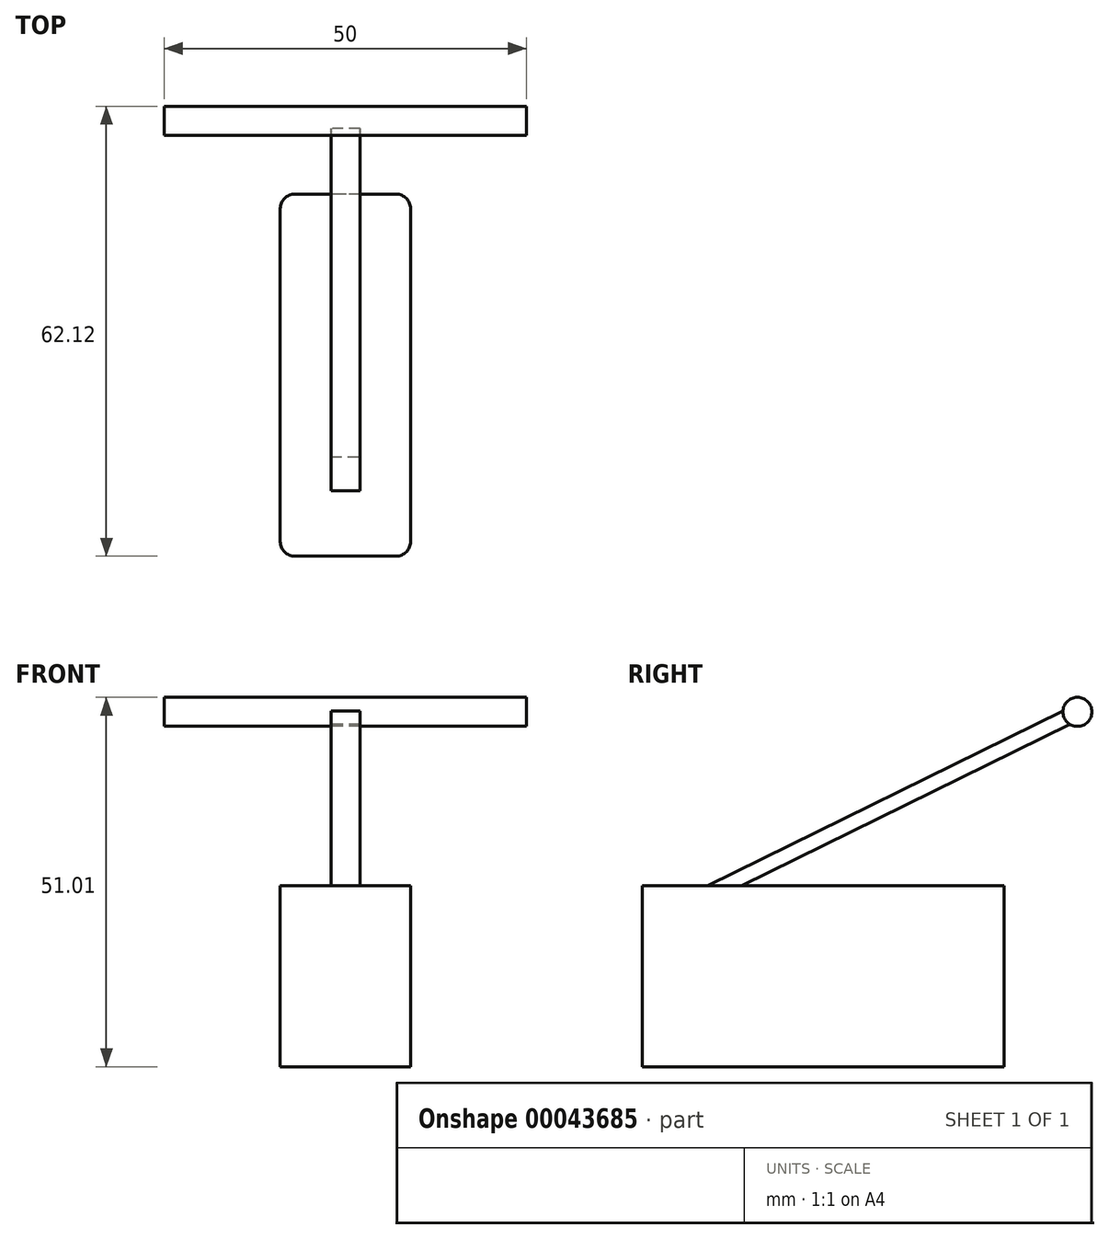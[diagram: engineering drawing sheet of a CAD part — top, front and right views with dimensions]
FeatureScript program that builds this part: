
annotation { "Feature Type Name" : "Feature", "Feature Type Description" : "" }
export const myFeature = defineFeature(function(context is Context, id is Id, definition is map)
    precondition{}
    {
        {
            var Q0;
            Q0=qCreatedBy(makeId("Top.planeOp"),FACE);
            var sketch = newSketch(context, id + "F0", { "sketchPlane" : qUnion([Q0])});
            skLineSegment(sketch, "E0.rect.bottom", {"start": v(7, -25) * mm, "end": v(-7, -25) * mm});
            skLineSegment(sketch, "E0.rect.top", {"start": v(7, 25) * mm, "end": v(-7, 25) * mm});
            skLineSegment(sketch, "E0.rect.left", {"start": v(9, -23) * mm, "end": v(9, 23) * mm});
            skLineSegment(sketch, "E0.rect.right", {"start": v(-9, -23) * mm, "end": v(-9, 23) * mm});
            skPoint(sketch, "E0.rect.middle", {"position": v(0, 0) * mm});
            skPoint(sketch, "E1.visualSharp", {"position": v(9, 25) * mm});
            skArc(sketch, "E1.filletArc", {"start": v(9, 23) * mm, "mid": v(8.41, 24.41) * mm, "end": v(7, 25) * mm});
            skPoint(sketch, "E2.visualSharp", {"position": v(-9, 25) * mm});
            skArc(sketch, "E2.filletArc", {"start": v(-7, 25) * mm, "mid": v(-8.41, 24.41) * mm, "end": v(-9, 23) * mm});
            skPoint(sketch, "E3.visualSharp", {"position": v(-9, -25) * mm});
            skArc(sketch, "E3.filletArc", {"start": v(-9, -23) * mm, "mid": v(-8.41, -24.41) * mm, "end": v(-7, -25) * mm});
            skPoint(sketch, "E4.visualSharp", {"position": v(9, -25) * mm});
            skArc(sketch, "E4.filletArc", {"start": v(7, -25) * mm, "mid": v(8.41, -24.41) * mm, "end": v(9, -23) * mm});
            skSolve(sketch);
        }
        {
            var Q0;
            Q0=makeQuery(id+"F0.imprint","IMPRINT",FACE,{"disambiguationData":[TD([[makeQuery(id+"F0.imprint","IMPRINT",EDGE,{"derivedFrom":sQuery(id+"F0.wireOp",EDGE,"E0.rect.bottom")}),-1.0]])]});
            extrude(context, id + "F1", {"entities" : qUnion([Q0]), "depth" : 25 * mm});
        }
        {
            var Q0;
            Q0=makeQuery(id+"F1.opExtrude","SWEPT_FACE",FACE,{"disambiguationData":[OSD([sQuery(id+"F0.wireOp",EDGE,"E0.rect.left")])]});
            var sketch = newSketch(context, id + "F2", { "sketchPlane" : qUnion([Q0])});
            skLineSegment(sketch, "E5", {"start": v(-15.96, 25) * mm, "end": v(34.68, 49.9) * mm});
            skLineSegment(sketch, "E6", {"start": v(34.68, 49.9) * mm, "end": v(35.58, 48.06) * mm});
            skLineSegment(sketch, "E7", {"start": v(35.58, 48.06) * mm, "end": v(-11.3, 25) * mm});
            skSolve(sketch);
        }
        {
            var Q0;
            {var subQ2=sQuery(id+"F2.wireOp",EDGE,"E5");Q0=makeQuery(id+"F2.imprint","IMPRINT",FACE,{"disambiguationData":[TD([[makeQuery(id+"F2.imprint","IMPRINT",EDGE,{"derivedFrom":subQ2}),-1.0]])]});}
            extrude(context, id + "F3", {"entities" : qUnion([Q0]), "operationType" : NewBodyOperationType.ADD, "oppositeDirection" : true, "depth" : 11 * mm, "hasSecondDirection" : true, "secondDirectionOppositeDirection" : true, "secondDirectionDepth" : 7 * mm});
        }
        {
            var Q0;
            Q0=makeQuery(id+"F3.opExtrude","SWEPT_FACE",FACE,{"disambiguationData":[OSD([sQuery(id+"F2.wireOp",EDGE,"E6")])]});
            var sketch = newSketch(context, id + "F4", { "sketchPlane" : qUnion([Q0])});
            skLineSegment(sketch, "E8.rect.bottom", {"start": v(25, 28.48) * mm, "end": v(-25, 28.48) * mm});
            skLineSegment(sketch, "E8.rect.top", {"start": v(25, 30.48) * mm, "end": v(-25, 30.48) * mm});
            skLineSegment(sketch, "E8.rect.left", {"start": v(25, 28.48) * mm, "end": v(25, 30.48) * mm});
            skLineSegment(sketch, "E8.rect.right", {"start": v(-25, 28.48) * mm, "end": v(-25, 30.48) * mm});
            skPoint(sketch, "E8.rect.middle", {"position": v(0, 29.48) * mm});
            skSolve(sketch);
        }
        {
            var Q0;
            {var subQ0=sQuery(id+"F2.wireOp",EDGE,"E6");var subQ4=makeQuery(id+"F3.opExtrude","SWEPT_EDGE",EDGE,{"disambiguationData":[OSD([sQuery(id+"F2.wireOp",EDGE,"E5"),subQ0])]});Q0=makeQuery(id+"F4.imprint","IMPRINT",FACE,{"disambiguationData":[TD([[makeQuery(id+"F4.imprint","IMPRINT",EDGE,{"derivedFrom":subQ4}),1.0]])]});}
            var Q1;
            Q1=makeQuery(id+"F4.imprint","IMPRINT",FACE,{"disambiguationData":[TD([[makeQuery(id+"F4.imprint","IMPRINT",EDGE,{"derivedFrom":sQuery(id+"F4.wireOp",EDGE,"E8.rect.top")}),1.0]])]});
            var Q2;
            Q2=sQuery(id+"F4.wireOp",EDGE,"E8.rect.bottom");
            revolve(context, id + "F5", {"operationType" : NewBodyOperationType.ADD, "entities" : qUnion([Q0, Q1]), "axis" : qUnion([Q2]), "revolveType" : RevolveType.FULL});
        }
    });
